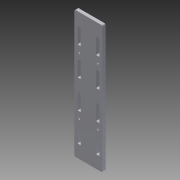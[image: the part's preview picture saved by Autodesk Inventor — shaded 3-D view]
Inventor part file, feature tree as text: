
AUTODESK INVENTOR PART (.ipt)
format: ipt  version: 2015 (Build 190159000, 159)  size: 153,600 bytes
history: native  units: mm
features: extrude x3, sketch x3, plane x2, mirror x2, fillet x1
ambient origin geometry x8: Origin, YZ Plane, XZ Plane, XY Plane, X Axis, Y Axis, Z Axis, Center Point
bodies: Solid1 (feature_tree)
feature tree (11):
  extrude  "Extrusion1"  Depth=44.0mm
  extrude  "Extrusion2"  Depth=200.0mm
  plane  "Work Plane1"
  plane  "Work Plane2"
  mirror  "Mirror1"
  mirror  "Mirror2"
  extrude  "Extrusion4"  Depth=2.0mm
  fillet  "Fillet1"  Radius=5.0mm
  sketch  "Sketch1"  dims[d0=200.0mm d1=44.0mm]
  sketch  "Sketch2"  dims[d2=5.0mm d3=0.0mm d4=200.0mm]
  sketch  "Sketch5"  dims[d5=20.0mm d6=108.0mm d8=5.0mm d9=5.0mm d10=10.0mm d11=25.0mm d12=20.0mm d13=25.0mm d14=10.0mm d15=25.0mm d16=20.0mm d17=25.0mm d18=20.0mm d19=25.0mm d20=20.0mm d21=25.0mm d22=5.0mm d23=0.0mm d24=-22.0mm d25=-100.0mm d41=5.0mm d42=3.2mm d43=10.0mm d44=2.5mm d45=5.0mm d46=0.0mm d47=2.0mm]
